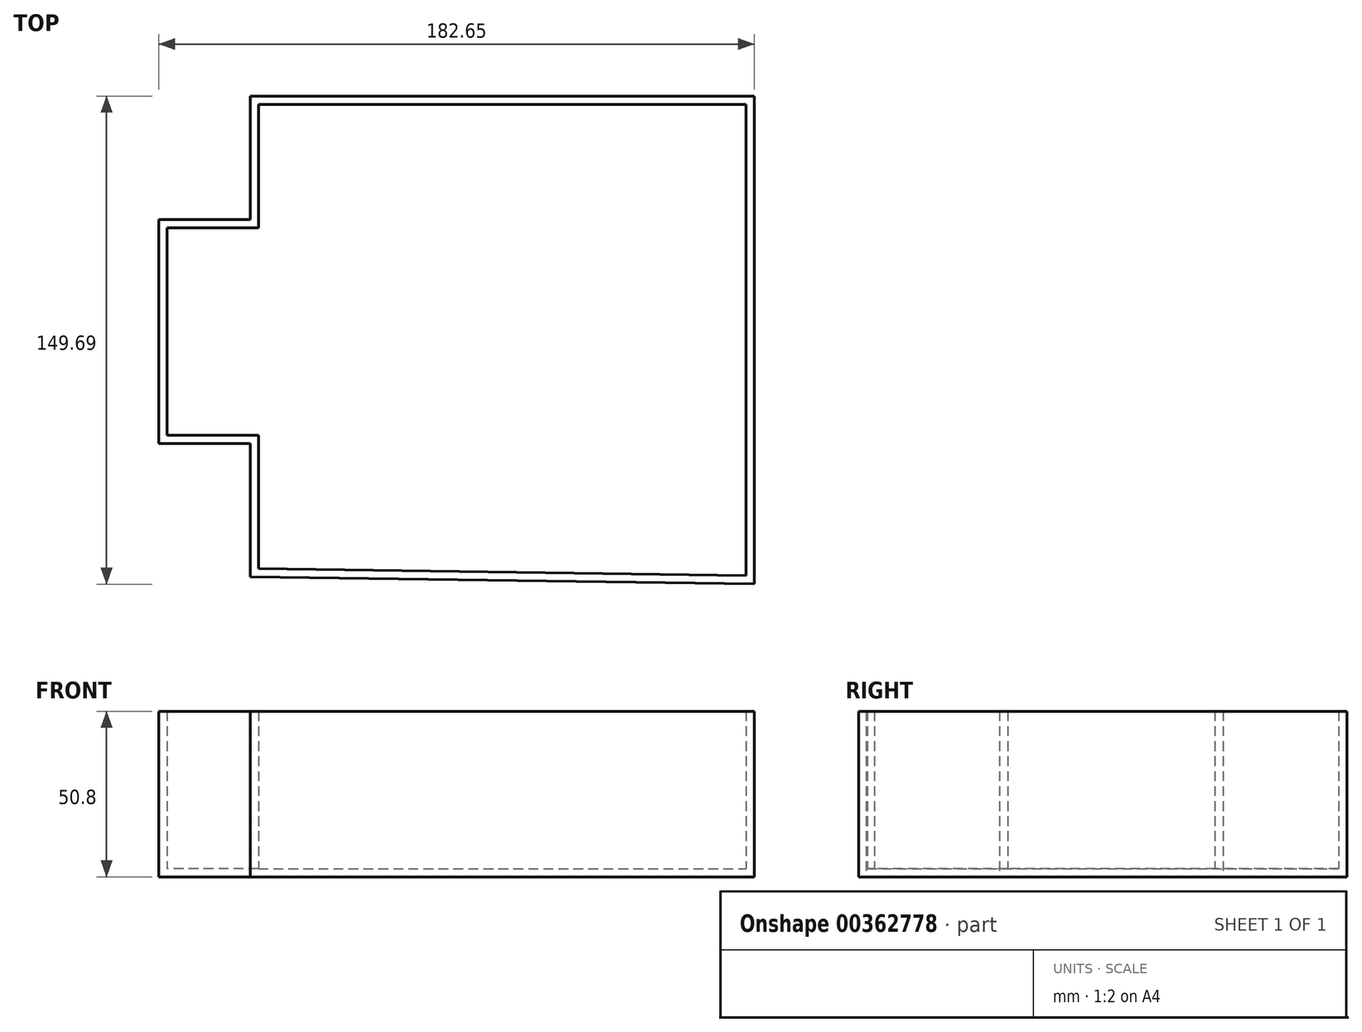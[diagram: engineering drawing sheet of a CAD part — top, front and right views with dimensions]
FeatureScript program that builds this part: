
annotation { "Feature Type Name" : "Feature", "Feature Type Description" : "" }
export const myFeature = defineFeature(function(context is Context, id is Id, definition is map)
    precondition{}
    {
        {
            var Q0;
            Q0=qCreatedBy(makeId("Top.planeOp"),FACE);
            var sketch = newSketch(context, id + "F0", { "sketchPlane" : qUnion([Q0])});
            skLineSegment(sketch, "E0", {"start": v(-35.2, 0) * mm, "end": v(-35.2, 0) * mm});
            skLineSegment(sketch, "E1", {"start": v(80.82, -76.24) * mm, "end": v(80.82, 73.45) * mm});
            skLineSegment(sketch, "E2", {"start": v(80.82, 73.45) * mm, "end": v(-73.82, 73.45) * mm});
            skLineSegment(sketch, "E3", {"start": v(-73.82, 73.45) * mm, "end": v(-73.82, 35.54) * mm});
            skLineSegment(sketch, "E4", {"start": v(-73.82, 35.54) * mm, "end": v(-101.83, 35.54) * mm});
            skLineSegment(sketch, "E5", {"start": v(-101.83, 35.54) * mm, "end": v(-101.83, -33.13) * mm});
            skLineSegment(sketch, "E6", {"start": v(-101.83, -33.13) * mm, "end": v(-73.82, -33.13) * mm});
            skLineSegment(sketch, "E7", {"start": v(-73.82, -33.13) * mm, "end": v(-73.82, -73.98) * mm});
            skLineSegment(sketch, "E8", {"start": v(-73.82, -73.98) * mm, "end": v(80.82, -76.24) * mm});
            skSolve(sketch);
        }
        {
            var Q0;
            Q0 = qSketchRegion(id + "F0", true);
            extrude(context, id + "F1", {"entities" : qUnion([Q0]), "depth" : 50.8 * mm});
        }
        {
            var Q0;
            Q0=makeQuery(id+"F1.opExtrude","CAP_FACE",FACE,{"disambiguationData":[OSD([sQuery(id+"F0.wireOp",EDGE,"E1"),sQuery(id+"F0.wireOp",EDGE,"E2"),sQuery(id+"F0.wireOp",EDGE,"E3"),sQuery(id+"F0.wireOp",EDGE,"E4"),sQuery(id+"F0.wireOp",EDGE,"E5"),sQuery(id+"F0.wireOp",EDGE,"E6"),sQuery(id+"F0.wireOp",EDGE,"E7"),sQuery(id+"F0.wireOp",EDGE,"E8")])],"isStart":false});
            shell(context, id + "F2", {"entities" : qUnion([Q0]), "thickness" : 2.54 * mm});
        }
    });
